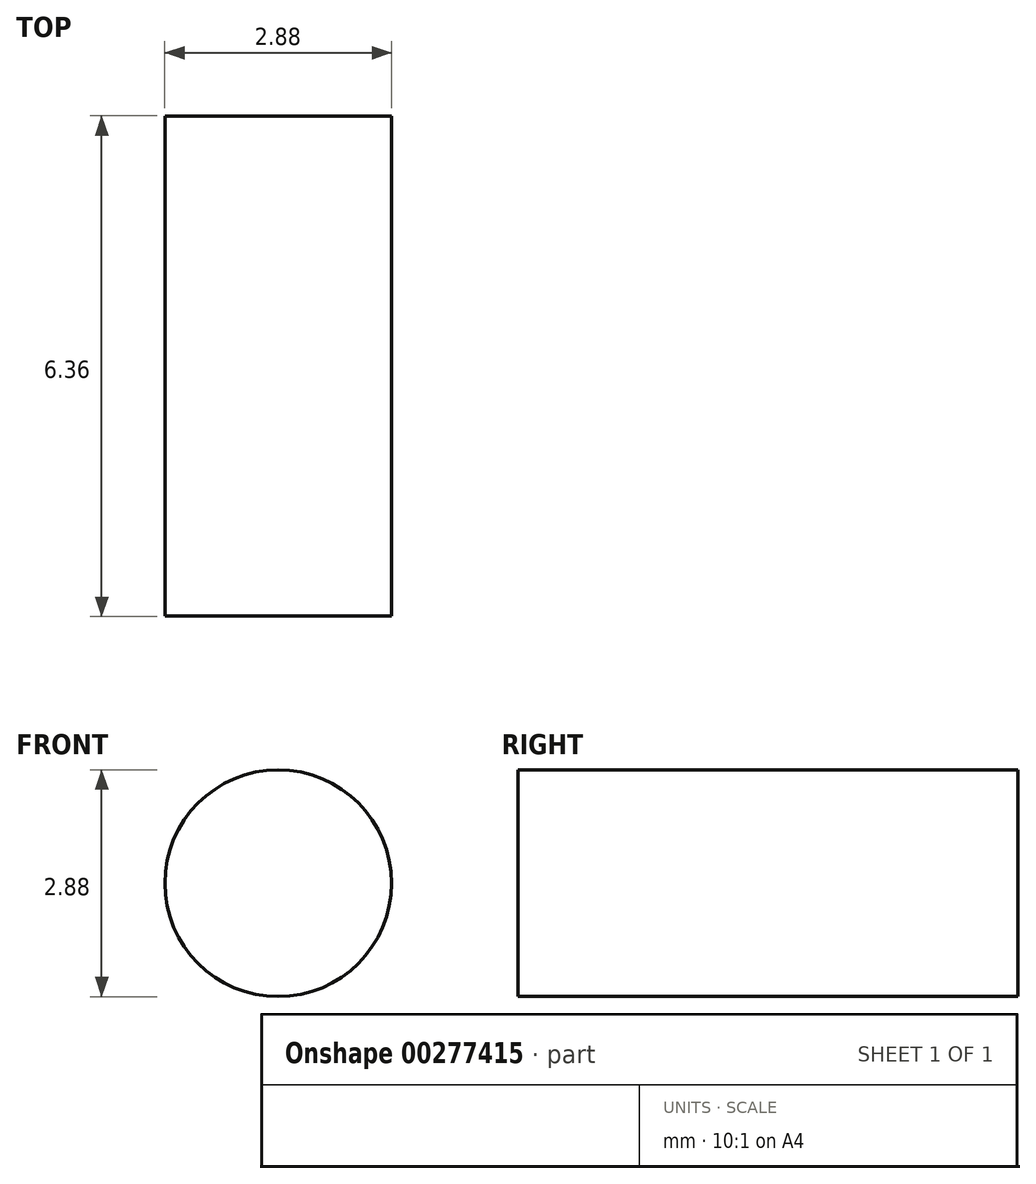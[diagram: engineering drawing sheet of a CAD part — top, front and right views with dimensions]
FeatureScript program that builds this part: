
annotation { "Feature Type Name" : "Feature", "Feature Type Description" : "" }
export const myFeature = defineFeature(function(context is Context, id is Id, definition is map)
    precondition{}
    {
        {
            var Q0;
            Q0=qCreatedBy(makeId("Front.planeOp"),FACE);
            var sketch = newSketch(context, id + "F0", { "sketchPlane" : qUnion([Q0])});
            skCircle(sketch, "E0", {"center": v(-5.54, 5.12) * mm, "radius": 1.44 * mm});
            skSolve(sketch);
        }
        {
            var Q0;
            Q0 = qSketchRegion(id + "F0", true);
            extrude(context, id + "F1", {"entities" : qUnion([Q0]), "depth" : 3.17 * mm, "hasSecondDirection" : true, "secondDirectionOppositeDirection" : true, "secondDirectionDepth" : 3.17 * mm});
        }
    });
